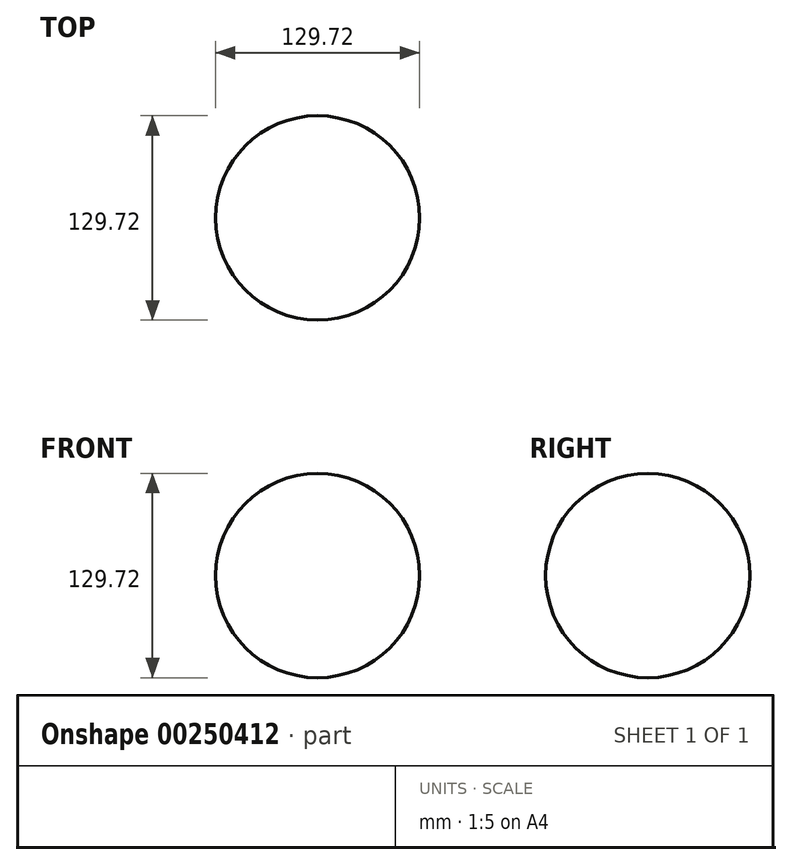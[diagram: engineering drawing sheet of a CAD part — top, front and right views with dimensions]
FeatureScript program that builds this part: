
annotation { "Feature Type Name" : "Feature", "Feature Type Description" : "" }
export const myFeature = defineFeature(function(context is Context, id is Id, definition is map)
    precondition{}
    {
        {
            var Q0;
            Q0=qCreatedBy(makeId("Front.planeOp"),FACE);
            var sketch = newSketch(context, id + "F0", { "sketchPlane" : qUnion([Q0])});
            skLineSegment(sketch, "E0", {"start": v(0, 90.57) * mm, "end": v(0, -114.17) * mm, "construction": true});
            skArc(sketch, "E1", {"start": v(0, 64.86) * mm, "mid": v(-64.86, 0) * mm, "end": v(0, -64.86) * mm});
            skSolve(sketch);
        }
        {
            var Q0;
            Q0=sQuery(id+"F0.wireOp",EDGE,"E1");
            var Q1;
            Q1=sQuery(id+"F0.wireOp",EDGE,"E0");
            revolve(context, id + "F1", {"bodyType" : ToolBodyType.SURFACE, "surfaceEntities" : qUnion([Q0]), "axis" : qUnion([Q1]), "revolveType" : RevolveType.FULL});
        }
    });
